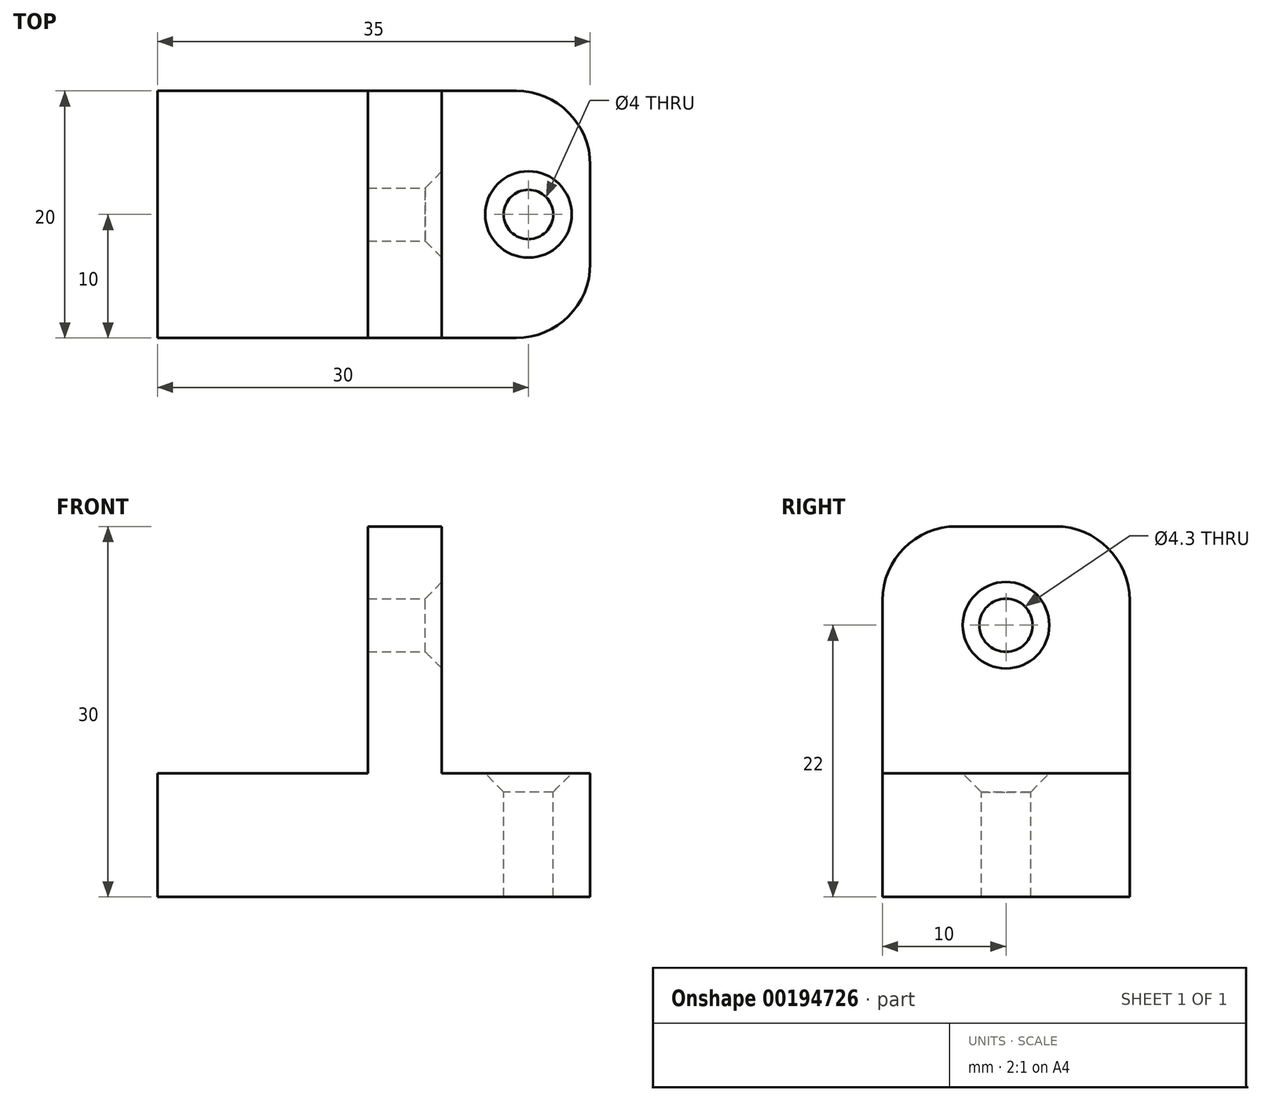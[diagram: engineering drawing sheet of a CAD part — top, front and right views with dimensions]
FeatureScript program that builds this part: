
annotation { "Feature Type Name" : "Feature", "Feature Type Description" : "" }
export const myFeature = defineFeature(function(context is Context, id is Id, definition is map)
    precondition{}
    {
        {
            var Q0;
            Q0=qCreatedBy(makeId("Top.planeOp"),FACE);
            var sketch = newSketch(context, id + "F0", { "sketchPlane" : qUnion([Q0])});
            skLineSegment(sketch, "E0.bottom", {"start": v(17.5, 10) * mm, "end": v(-17.5, 10) * mm});
            skLineSegment(sketch, "E0.top", {"start": v(17.5, -10) * mm, "end": v(-17.5, -10) * mm});
            skLineSegment(sketch, "E0.left", {"start": v(17.5, 10) * mm, "end": v(17.5, -10) * mm});
            skLineSegment(sketch, "E0.right", {"start": v(-17.5, 10) * mm, "end": v(-17.5, -10) * mm});
            skPoint(sketch, "E0.middle", {"position": v(0, 0) * mm});
            skLineSegment(sketch, "E1", {"start": v(17.5, 0) * mm, "end": v(12.5, 0) * mm});
            skPoint(sketch, "E1.endSnap0", {"position": v(17.5, 0) * mm});
            skCircle(sketch, "E2", {"center": v(12.5, 0) * mm, "radius": 2 * mm});
            skSolve(sketch);
        }
        {
            var Q0;
            Q0 = qSketchRegion(id + "F0", true);
            extrude(context, id + "F1", {"entities" : qUnion([Q0]), "oppositeDirection" : true, "depth" : 10 * mm});
        }
        {
            var Q0;
            Q0=makeQuery(id+"F1.opExtrude","CAP_FACE",FACE,{"disambiguationData":[OSD([sQuery(id+"F0.wireOp",EDGE,"E0.bottom"),sQuery(id+"F0.wireOp",EDGE,"E0.top"),sQuery(id+"F0.wireOp",EDGE,"E0.left"),sQuery(id+"F0.wireOp",EDGE,"E0.right"),sQuery(id+"F0.wireOp",EDGE,"E2")])],"isStart":true});
            var sketch = newSketch(context, id + "F2", { "sketchPlane" : qUnion([Q0])});
            skLineSegment(sketch, "E3", {"start": v(5.5, 10) * mm, "end": v(5.5, -10) * mm});
            skLineSegment(sketch, "E4", {"start": v(5.5, -10) * mm, "end": v(-0.5, -10) * mm});
            skLineSegment(sketch, "E5", {"start": v(-0.5, -10) * mm, "end": v(-0.5, 10) * mm});
            skLineSegment(sketch, "E6", {"start": v(-0.5, 10) * mm, "end": v(5.5, 10) * mm});
            skSolve(sketch);
        }
        {
            var Q0;
            Q0 = qSketchRegion(id + "F2", true);
            extrude(context, id + "F3", {"entities" : qUnion([Q0]), "operationType" : NewBodyOperationType.ADD, "depth" : 20 * mm});
        }
        {
            var Q0;
            Q0=makeQuery(id+"F3.opExtrude","SWEPT_FACE",FACE,{"disambiguationData":[OSD([sQuery(id+"F2.wireOp",EDGE,"E3")])]});
            var sketch = newSketch(context, id + "F4", { "sketchPlane" : qUnion([Q0])});
            skPoint(sketch, "E7.endSnap0", {"position": v(-10, 10) * mm});
            skLineSegment(sketch, "E8", {"start": v(0, 0) * mm, "end": v(0, 12) * mm, "construction": true});
            skPoint(sketch, "E8.endSnap0", {"position": v(0, 0) * mm});
            skCircle(sketch, "E9", {"center": v(0, 12) * mm, "radius": 2.15 * mm});
            skSolve(sketch);
        }
        {
            var Q0;
            Q0 = qSketchRegion(id + "F4", true);
            extrude(context, id + "F5", {"entities" : qUnion([Q0]), "operationType" : NewBodyOperationType.REMOVE, "oppositeDirection" : true, "depth" : 25 * mm});
        }
        {
            var Q0;
            Q0=makeQuery(id+"F3.opExtrude","CAP_EDGE",EDGE,{"disambiguationData":[OSD([sQuery(id+"F2.wireOp",EDGE,"E4")])],"isStart":false});
            var Q1;
            Q1=makeQuery(id+"F3.opExtrude","CAP_EDGE",EDGE,{"disambiguationData":[OSD([sQuery(id+"F2.wireOp",EDGE,"E6")])],"isStart":false});
            var Q2;
            Q2=makeQuery(id+"F1.opExtrude","SWEPT_EDGE",EDGE,{"disambiguationData":[OSD([sQuery(id+"F0.wireOp",EDGE,"E0.bottom"),sQuery(id+"F0.wireOp",EDGE,"E0.left")])]});
            var Q3;
            Q3=makeQuery(id+"F1.opExtrude","SWEPT_EDGE",EDGE,{"disambiguationData":[OSD([sQuery(id+"F0.wireOp",EDGE,"E0.top"),sQuery(id+"F0.wireOp",EDGE,"E0.left")])]});
            fillet(context, id + "F6", {"entities" : qUnion([Q0, Q1, Q2, Q3]), "radius" : 6 * mm, "tangentPropagation" : true, "allowEdgeOverflow" : false});
        }
        {
            var Q0;
            Q0=makeQuery(id+"F3.opExtrude","SWEPT_FACE",FACE,{"disambiguationData":[OSD([sQuery(id+"F2.wireOp",EDGE,"E3")])]});
            var sketch = newSketch(context, id + "F7", { "sketchPlane" : qUnion([Q0])});
            skPoint(sketch, "E10", {"position": v(0, 12) * mm});
            skSolve(sketch);
        }
        {
            var Q0;
            Q0=sQuery(id+"F7.wireOp",VERTEX,"E10");
            var Q1;
            Q1=makeQuery(id+"F1.opExtrude","SWEPT_BODY",BODY,{"disambiguationData":[OSD([sQuery(id+"F0.wireOp",EDGE,"E0.bottom"),sQuery(id+"F0.wireOp",EDGE,"E0.top"),sQuery(id+"F0.wireOp",EDGE,"E0.left"),sQuery(id+"F0.wireOp",EDGE,"E0.right"),sQuery(id+"F0.wireOp",EDGE,"E2")])]});
            hole(context, id + "F8", {"style" : HoleStyle.C_SINK, "endStyle" : HoleEndStyle.BLIND, "holeDiameter" : 4 * mm, "cSinkDiameter" : 7 * mm, "cSinkAngle" : 90 * degree, "holeDepth" : 7 * mm, "isTappedThrough" : true, "tappedDepth" : 12 * mm, "tapClearance" : 3, "startFromSketch" : true, "locations" : qUnion([Q0]), "scope" : qUnion([Q1])});
        }
        {
            var Q0;
            {var subQ0=sQuery(id+"F0.wireOp",EDGE,"E2");var subQ1=sQuery(id+"F0.wireOp",EDGE,"E0.left");var subQ2=sQuery(id+"F0.wireOp",EDGE,"E0.top");var subQ3=sQuery(id+"F0.wireOp",EDGE,"E0.bottom");Q0=makeQuery(id+"F3.boolean.opBoolean","SPLIT",FACE,{"disambiguationData":[TD([makeQuery(id+"F1.opExtrude","SWEPT_FACE",FACE,{"disambiguationData":[OSD([subQ1])]})])],"derivedFrom":makeQuery(id+"F1.opExtrude","CAP_FACE",FACE,{"disambiguationData":[OSD([subQ3,subQ2,subQ1,sQuery(id+"F0.wireOp",EDGE,"E0.right"),subQ0])],"isStart":true})});}
            var sketch = newSketch(context, id + "F9", { "sketchPlane" : qUnion([Q0])});
            skPoint(sketch, "E11", {"position": v(12.5, 0) * mm});
            skSolve(sketch);
        }
        {
            var Q0;
            Q0=sQuery(id+"F9.wireOp",VERTEX,"E11");
            var Q1;
            Q1=makeQuery(id+"F1.opExtrude","SWEPT_BODY",BODY,{"disambiguationData":[OSD([sQuery(id+"F0.wireOp",EDGE,"E0.bottom"),sQuery(id+"F0.wireOp",EDGE,"E0.top"),sQuery(id+"F0.wireOp",EDGE,"E0.left"),sQuery(id+"F0.wireOp",EDGE,"E0.right"),sQuery(id+"F0.wireOp",EDGE,"E2")])]});
            hole(context, id + "F10", {"style" : HoleStyle.C_SINK, "endStyle" : HoleEndStyle.BLIND, "holeDiameter" : 4 * mm, "cSinkDiameter" : 7 * mm, "cSinkAngle" : 90 * degree, "holeDepth" : 12 * mm, "isTappedThrough" : true, "tappedDepth" : 12 * mm, "tapClearance" : 3, "startFromSketch" : true, "locations" : qUnion([Q0]), "scope" : qUnion([Q1])});
        }
    });
